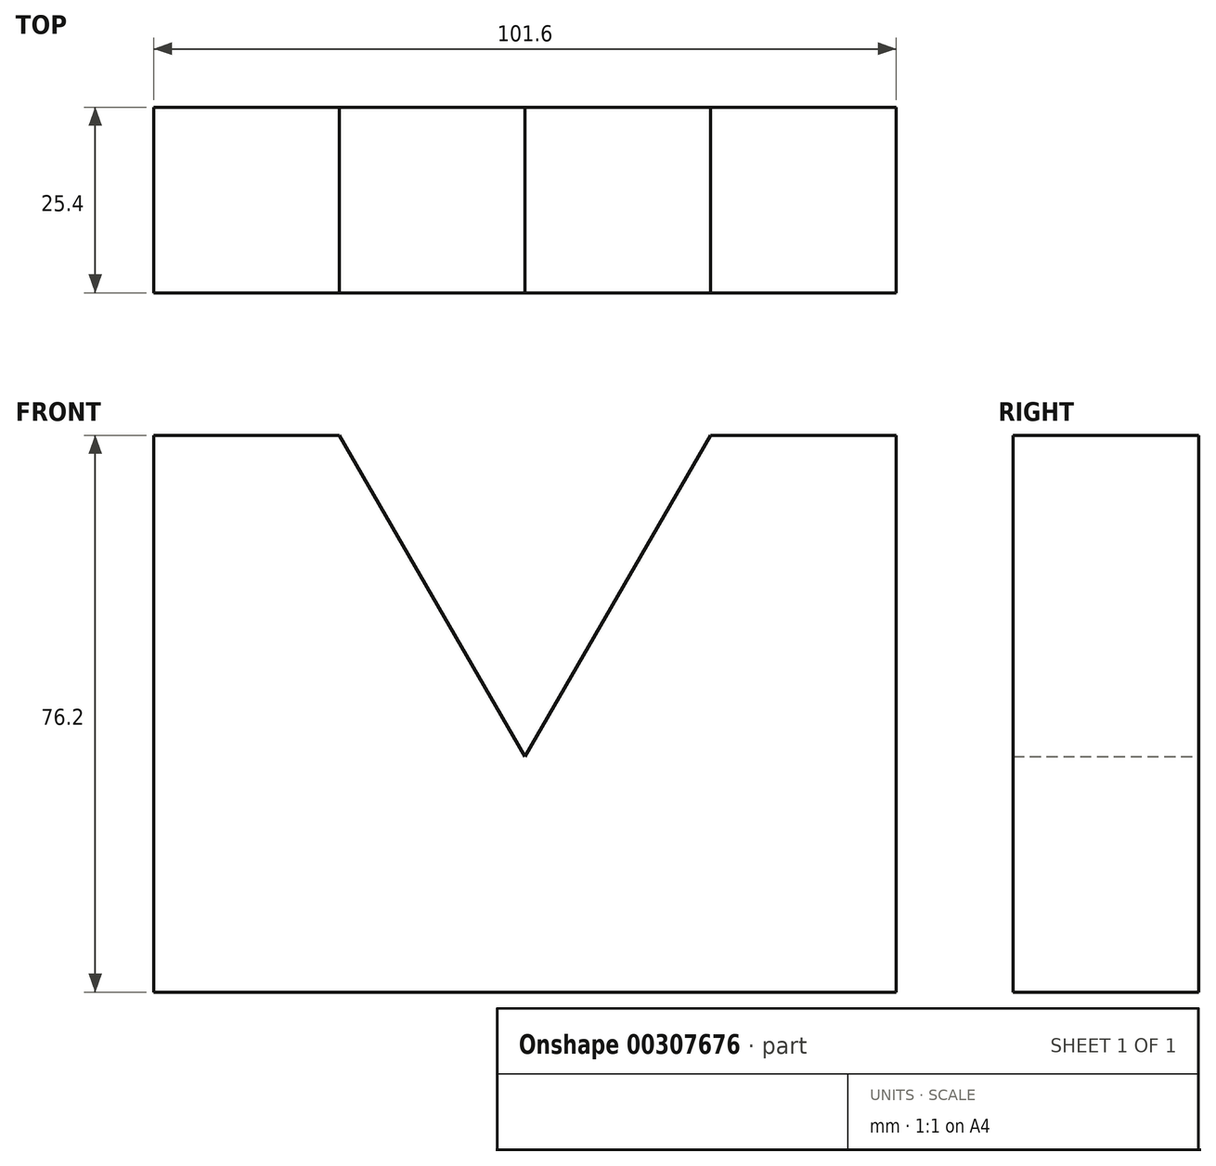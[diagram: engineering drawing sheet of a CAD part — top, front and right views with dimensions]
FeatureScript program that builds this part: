
annotation { "Feature Type Name" : "Feature", "Feature Type Description" : "" }
export const myFeature = defineFeature(function(context is Context, id is Id, definition is map)
    precondition{}
    {
        {
            var Q0;
            Q0=qCreatedBy(makeId("Front.planeOp"),FACE);
            var sketch = newSketch(context, id + "F0", { "sketchPlane" : qUnion([Q0])});
            skLineSegment(sketch, "E0", {"start": v(23.55, -49.1) * mm, "end": v(-78.05, -49.1) * mm});
            skLineSegment(sketch, "E1", {"start": v(-78.05, -49.1) * mm, "end": v(-78.05, 27.1) * mm});
            skLineSegment(sketch, "E2", {"start": v(-78.05, 27.1) * mm, "end": v(-52.65, 27.1) * mm});
            skLineSegment(sketch, "E3", {"start": v(-52.65, 27.1) * mm, "end": v(-27.25, -16.89) * mm});
            skLineSegment(sketch, "E4", {"start": v(-27.25, -16.89) * mm, "end": v(-1.85, 27.1) * mm});
            skLineSegment(sketch, "E5", {"start": v(-1.85, 27.1) * mm, "end": v(23.55, 27.1) * mm});
            skLineSegment(sketch, "E6", {"start": v(23.55, 27.1) * mm, "end": v(23.55, -49.1) * mm});
            skSolve(sketch);
        }
        {
            var Q0;
            Q0=makeQuery(id+"F0.imprint","IMPRINT",FACE,{"disambiguationData":[TD([[makeQuery(id+"F0.imprint","IMPRINT",EDGE,{"derivedFrom":sQuery(id+"F0.wireOp",EDGE,"E0")}),-1.0]])]});
            extrude(context, id + "F1", {"entities" : qUnion([Q0]), "depth" : 25.4 * mm});
        }
    });
